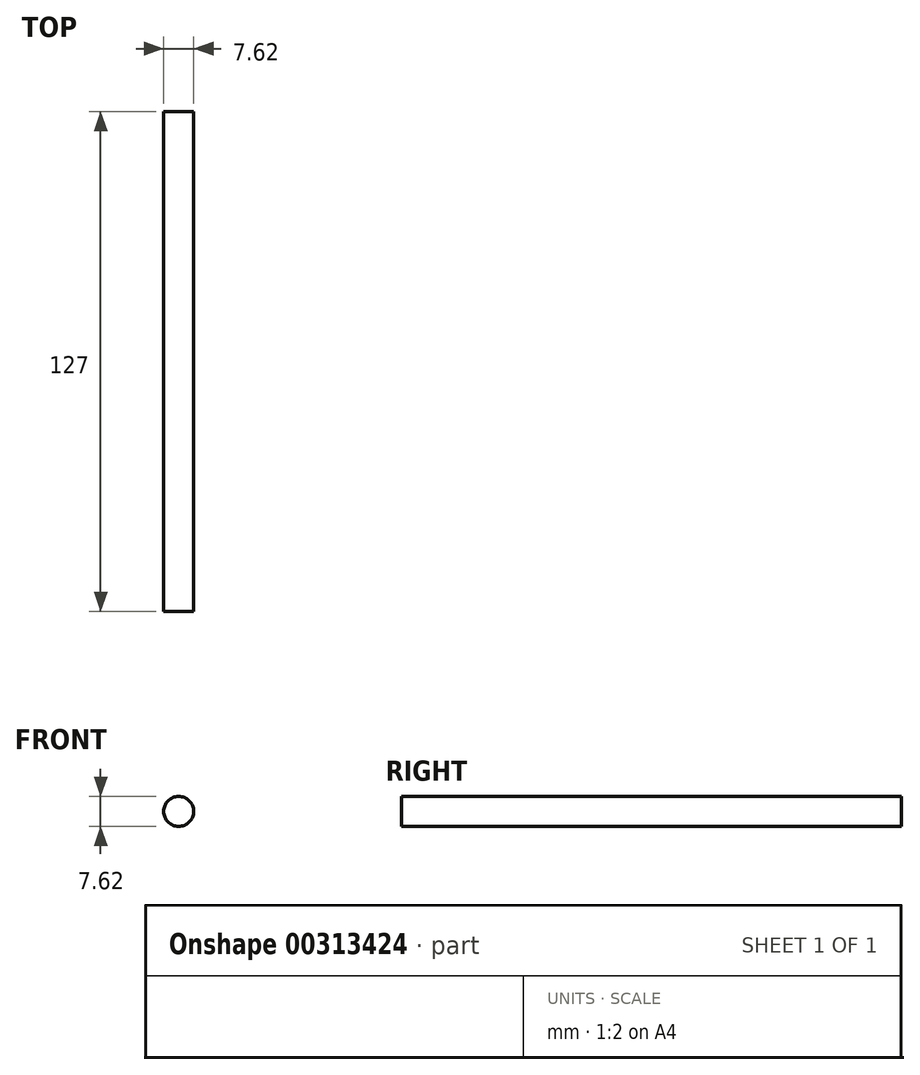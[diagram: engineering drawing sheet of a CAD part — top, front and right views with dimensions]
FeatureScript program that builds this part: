
annotation { "Feature Type Name" : "Feature", "Feature Type Description" : "" }
export const myFeature = defineFeature(function(context is Context, id is Id, definition is map)
    precondition{}
    {
        {
            var Q0;
            Q0=qCreatedBy(makeId("Front.planeOp"),FACE);
            var sketch = newSketch(context, id + "F0", { "sketchPlane" : qUnion([Q0])});
            skCircle(sketch, "E0", {"center": v(0, 0) * mm, "radius": 3.81 * mm});
            skSolve(sketch);
        }
        {
            var Q0;
            Q0 = qSketchRegion(id + "F0", true);
            extrude(context, id + "F1", {"entities" : qUnion([Q0]), "depth" : 127 * mm});
        }
    });
